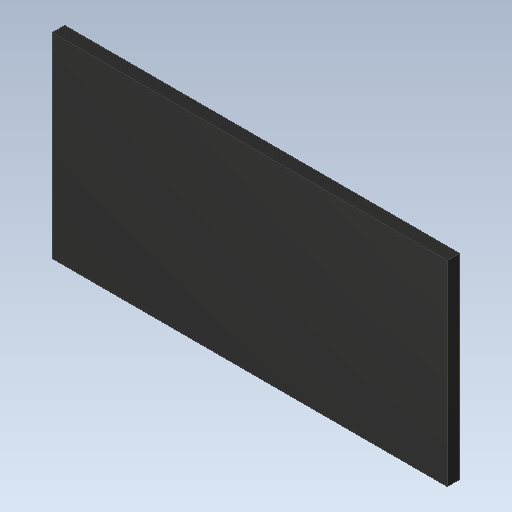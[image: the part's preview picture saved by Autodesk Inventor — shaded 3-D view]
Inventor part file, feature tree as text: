
AUTODESK INVENTOR PART (.ipt)
format: ipt  version: 2020 (Build 240168000, 168)  size: 87,040 bytes
history: imported  units: in
note: dims shown in document units (in); Inventor stores cm internally (conversion verified against a paired STEP export)
features: imported_body x1
ambient origin geometry x8: Origin, YZ Plane, XZ Plane, XY Plane, X Axis, Y Axis, Z Axis, Center Point
bodies: Solid1 (imported_parasolid), Body1 (imported_parasolid)
feature tree (1):
  imported_body  NMx_Import_Brep_tag  [imported B-rep: ~6 faces, bbox_mm=[3.227, 1.6, 0.1]]
